# Revit family: LBTYP001
name_source: partatom
category: Furniture
units: mm (PartAtom-declared; Revit-internal decimal feet)

## family parameters
Always vertical = Yes
Cut with Voids When Loaded = No
OmniClass Number = 23.40.20.00
OmniClass Title = General Furniture and Specialties
Render Appearance Source = Family Geometry
Room Calculation Point = No
Shared = No
Work Plane-Based = No

## types (1)
- LBTYP001
    Cost = 38441 $
    Default Elevation = 0 mm  [stored 0 ft]
    Description = 1 x Chatham Cove 3-Sided Right Non-Powered 50h x 42w x 30d, 1 x Chatham Cove 3-Sided Left Powered 50h x 42w x 30d, 4 x Volker Cube w/Casters - 18x18x18, 4 x LB LOUNGE, BACKLESS, 30 WIDTH CLOSED BOTTOM, 2 x LB LOUNGE, CORNER, 50 TALL, SOLID BASE, REAR OVERLAY, LEFT, 2 x LB Lounge 1 Seat 50H X 30W X 30 Open Base, 1 x LB LOUNGE 2 SEAT 50"H X 42"W X 30" SOLID BASE, 2 x Chatham Cove Insert PET  50 x 30, 1 x COLLAB TBL, KEY TOP, 2mm, 36Dx60Wx29H, DISC, 4 x Laptop Table, 4 x Calibrate Dry Planter 50Hx30Wx12D, 1 x Collaborative Table Wall Mount Kit (4 Black Brackets)
    Exported From CET Designer = Yes
    Manufacturer = AIS
    Model = F-CC3NR504230
    Show LBTYP001 = Yes
    VisibilityIndex = 0

note: [stored X ft] marks values corroborated as IEEE doubles in the binary element streams (Revit-internal decimal feet)

## geometry (parser evidence)
native form markers: Sweep x2
no freeform markers — native parametric forms only
